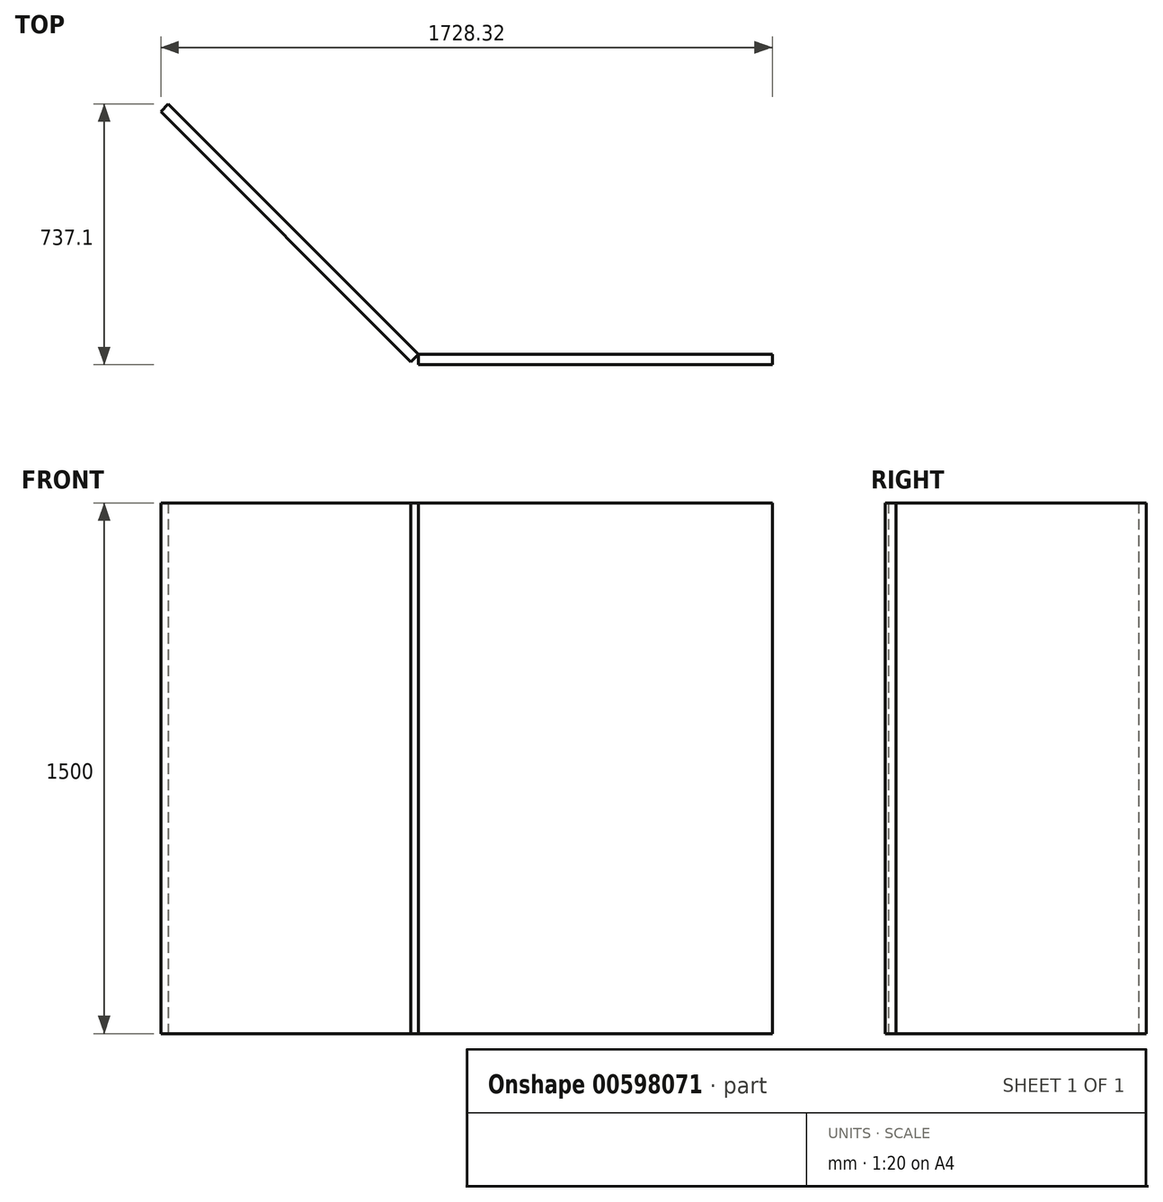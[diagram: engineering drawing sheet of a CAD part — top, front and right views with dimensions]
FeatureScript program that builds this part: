
annotation { "Feature Type Name" : "Feature", "Feature Type Description" : "" }
export const myFeature = defineFeature(function(context is Context, id is Id, definition is map)
    precondition{}
    {
        {
            var Q0;
            Q0=qCreatedBy(makeId("Top.planeOp"),FACE);
            var sketch = newSketch(context, id + "F0", { "sketchPlane" : qUnion([Q0])});
            skLineSegment(sketch, "E0.bottom", {"start": v(-156.9, -228.84) * mm, "end": v(843.1, -228.84) * mm});
            skLineSegment(sketch, "E0.top", {"start": v(-156.9, -258.84) * mm, "end": v(843.1, -258.84) * mm});
            skLineSegment(sketch, "E0.left", {"start": v(-156.9, -228.84) * mm, "end": v(-156.9, -258.84) * mm});
            skLineSegment(sketch, "E0.right", {"start": v(843.1, -228.84) * mm, "end": v(843.1, -258.84) * mm});
            skLineSegment(sketch, "E1", {"start": v(-156.9, -228.84) * mm, "end": v(-864.01, 478.26) * mm});
            skLineSegment(sketch, "E2", {"start": v(-864.01, 478.26) * mm, "end": v(-885.22, 457.05) * mm});
            skLineSegment(sketch, "E3", {"start": v(-885.22, 457.05) * mm, "end": v(-178.12, -250.06) * mm});
            skLineSegment(sketch, "E4", {"start": v(-178.12, -250.06) * mm, "end": v(-156.9, -228.84) * mm});
            skSolve(sketch);
        }
        {
            var Q0;
            Q0=qSketchRegion(id+"F0",true);
            extrude(context, id + "F1", {"entities" : qUnion([Q0]), "depth" : 1500 * mm, "offsetDistance" : 25 * mm});
        }
    });
